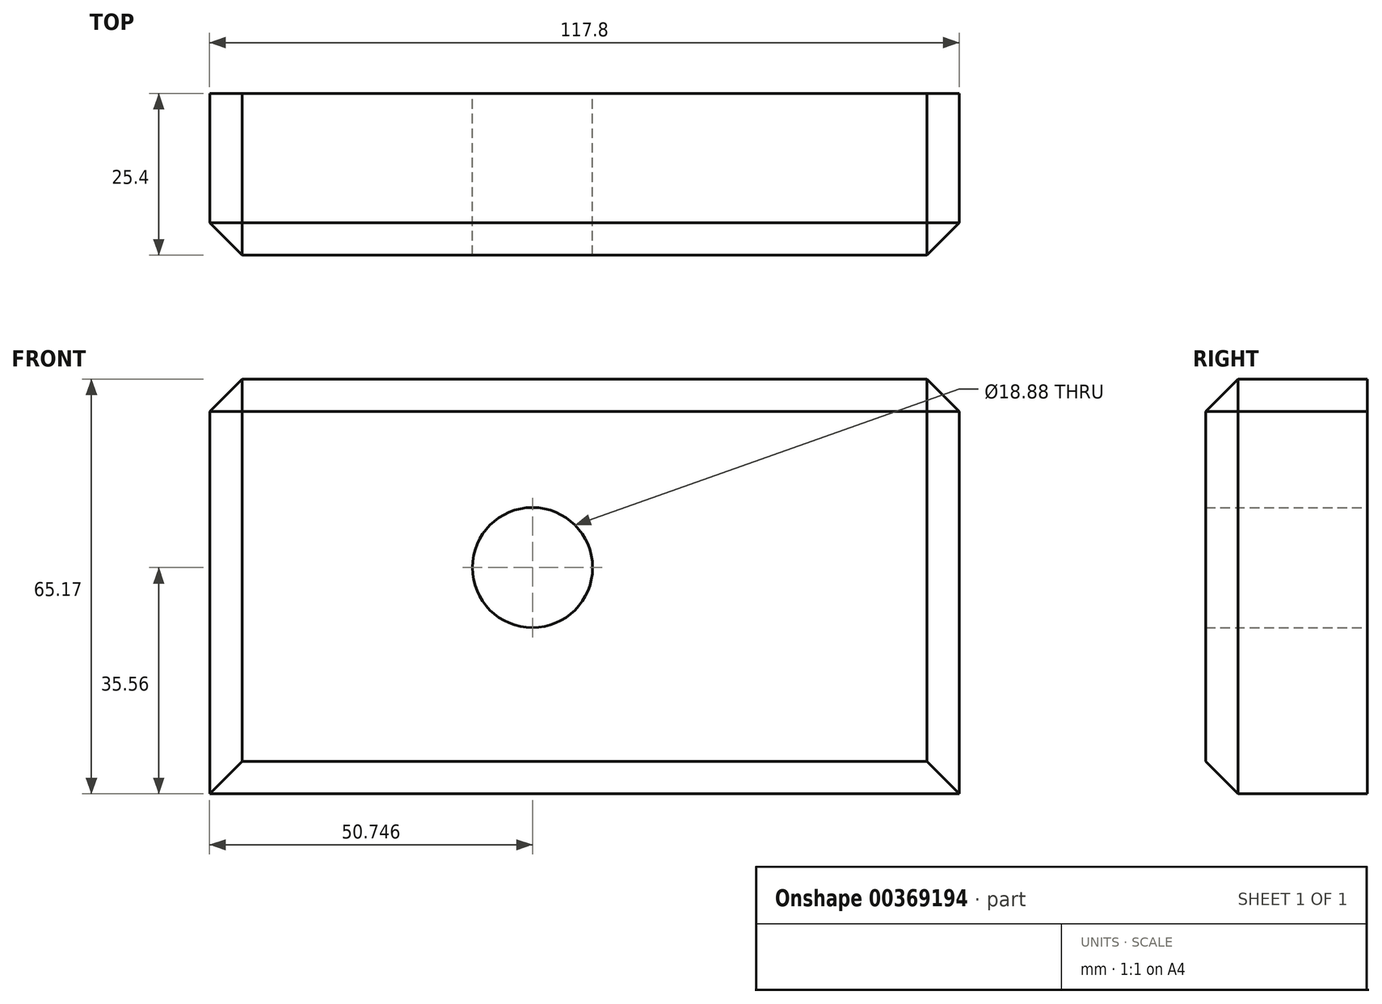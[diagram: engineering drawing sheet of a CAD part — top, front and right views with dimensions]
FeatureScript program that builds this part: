
annotation { "Feature Type Name" : "Feature", "Feature Type Description" : "" }
export const myFeature = defineFeature(function(context is Context, id is Id, definition is map)
    precondition{}
    {
        {
            var Q0;
            Q0=qCreatedBy(makeId("Front.planeOp"),FACE);
            var sketch = newSketch(context, id + "F0", { "sketchPlane" : qUnion([Q0])});
            skLineSegment(sketch, "E0.bottom", {"start": v(-66.53, 65.17) * mm, "end": v(51.27, 65.17) * mm});
            skLineSegment(sketch, "E0.top", {"start": v(-66.53, 0) * mm, "end": v(51.27, 0) * mm});
            skLineSegment(sketch, "E0.left", {"start": v(-66.53, 65.17) * mm, "end": v(-66.53, 0) * mm});
            skLineSegment(sketch, "E0.right", {"start": v(51.27, 65.17) * mm, "end": v(51.27, 0) * mm});
            skSolve(sketch);
        }
        {
            var Q0;
            Q0=makeQuery(id+"F0.imprint","IMPRINT",FACE,{"disambiguationData":[TD([[makeQuery(id+"F0.imprint","IMPRINT",EDGE,{"derivedFrom":sQuery(id+"F0.wireOp",EDGE,"E0.bottom")}),-1.0]])]});
            extrude(context, id + "F1", {"entities" : qUnion([Q0]), "depth" : 25.4 * mm});
        }
        {
            var Q0;
            Q0=makeQuery(id+"F1.opExtrude","SWEPT_EDGE",EDGE,{"disambiguationData":[OSD([sQuery(id+"F0.wireOp",EDGE,"E0.bottom"),sQuery(id+"F0.wireOp",EDGE,"E0.left")])]});
            var Q1;
            Q1=makeQuery(id+"F1.opExtrude","CAP_FACE",FACE,{"disambiguationData":[OSD([sQuery(id+"F0.wireOp",EDGE,"E0.bottom"),sQuery(id+"F0.wireOp",EDGE,"E0.top"),sQuery(id+"F0.wireOp",EDGE,"E0.left"),sQuery(id+"F0.wireOp",EDGE,"E0.right")])],"isStart":false});
            var Q2;
            Q2=makeQuery(id+"F1.opExtrude","SWEPT_EDGE",EDGE,{"disambiguationData":[OSD([sQuery(id+"F0.wireOp",EDGE,"E0.bottom"),sQuery(id+"F0.wireOp",EDGE,"E0.right")])]});
            chamfer(context, id + "F2", {"entities" : qUnion([Q0, Q1, Q2]), "width" : 5.08 * mm, "tangentPropagation" : true});
        }
        {
            var Q0;
            Q0=makeQuery(id+"F1.opExtrude","CAP_FACE",FACE,{"disambiguationData":[OSD([sQuery(id+"F0.wireOp",EDGE,"E0.bottom"),sQuery(id+"F0.wireOp",EDGE,"E0.top"),sQuery(id+"F0.wireOp",EDGE,"E0.left"),sQuery(id+"F0.wireOp",EDGE,"E0.right")])],"isStart":true});
            var sketch = newSketch(context, id + "F3", { "sketchPlane" : qUnion([Q0])});
            skCircle(sketch, "E1", {"center": v(15.78, 35.56) * mm, "radius": 9.44 * mm});
            skSolve(sketch);
        }
        {
            var Q0;
            Q0 = qSketchRegion(id + "F3", true);
            extrude(context, id + "F4", {"entities" : qUnion([Q0]), "operationType" : NewBodyOperationType.REMOVE, "endBound" : BoundingType.THROUGH_ALL, "oppositeDirection" : true, "depth" : 25.4 * mm});
        }
    });
